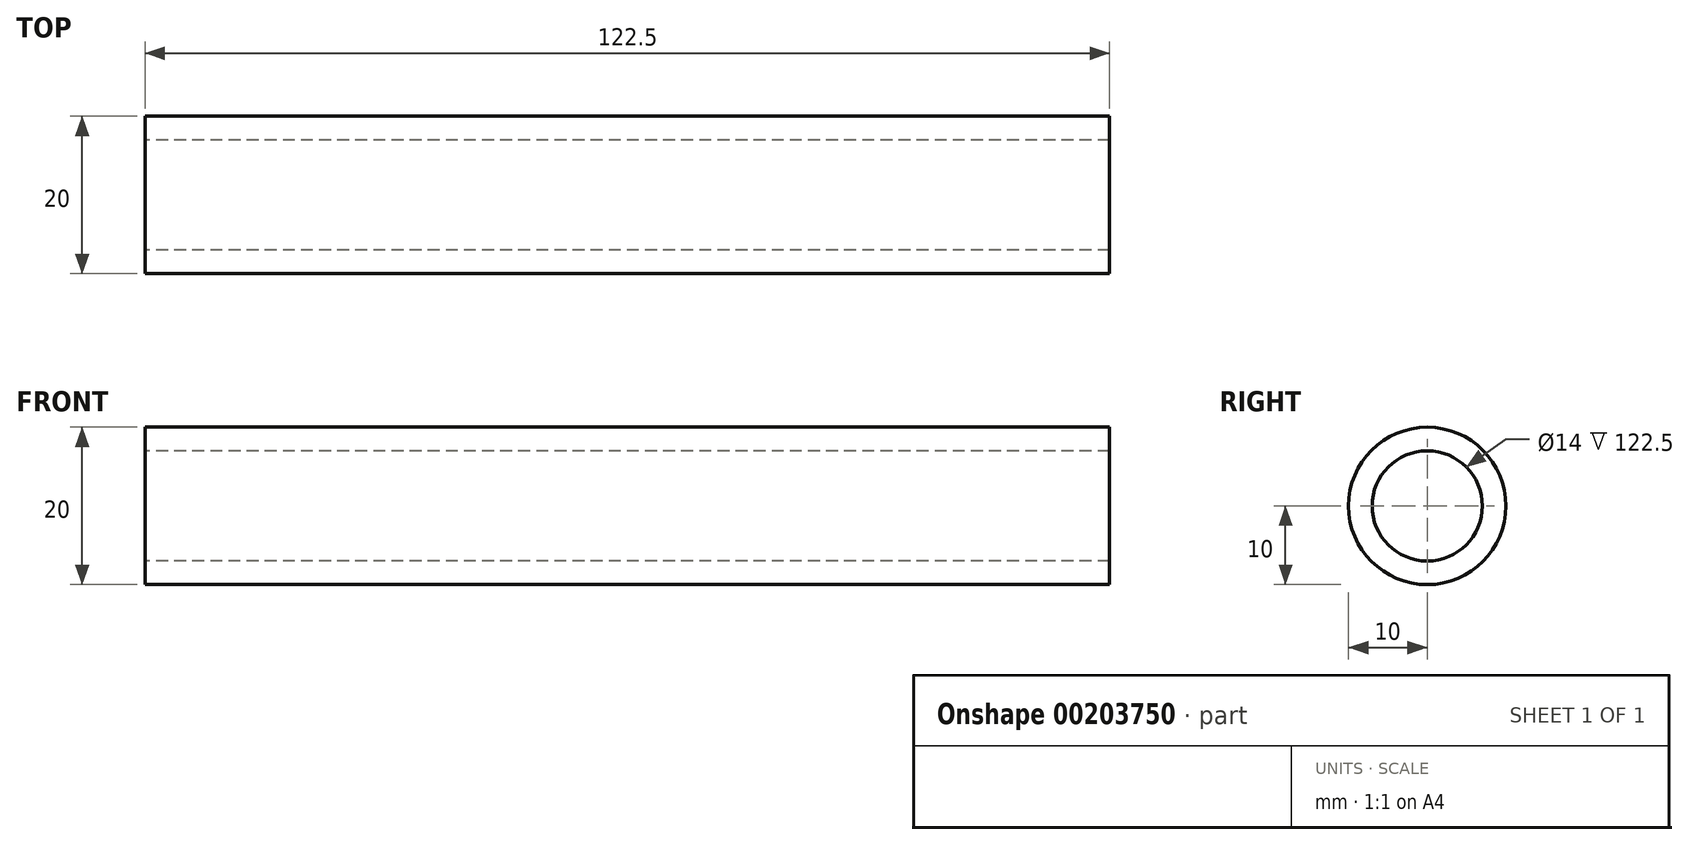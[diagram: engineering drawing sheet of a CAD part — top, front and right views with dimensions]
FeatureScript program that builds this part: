
annotation { "Feature Type Name" : "Feature", "Feature Type Description" : "" }
export const myFeature = defineFeature(function(context is Context, id is Id, definition is map)
    precondition{}
    {
        {
            var Q0;
            Q0=qCreatedBy(makeId("Right.planeOp"),FACE);
            var sketch = newSketch(context, id + "F0", { "sketchPlane" : qUnion([Q0])});
            skCircle(sketch, "E0", {"center": v(0, 0) * mm, "radius": 10 * mm});
            skCircle(sketch, "E1", {"center": v(0, 0) * mm, "radius": 7 * mm});
            skSolve(sketch);
        }
        {
            var Q0;
            Q0 = qSketchRegion(id + "F0", true);
            var Q1;
            Q1=makeQuery(id+"F0.imprint","IMPRINT",FACE,{"disambiguationData":[TD([[makeQuery(id+"F0.imprint","IMPRINT",EDGE,{"derivedFrom":sQuery(id+"F0.wireOp",EDGE,"E0")}),1.0]])]});
            extrude(context, id + "F1", {"entities" : qUnion([Q0, Q1]), "depth" : 122.5 * mm});
        }
    });
